# Revit family: Coat_Hook-Bobrick-Fino-B-9542
name_source: partatom
category: Specialty Equipment
revit_build: Autodesk Revit 2018 (Build: 20170223_1515(x64)
units: mm (PartAtom-declared; Revit-internal decimal feet)

## family parameters
Cut with Voids When Loaded = No
Host = Face
OmniClass Number = 23.40.20.21.31
OmniClass Title = Robe Hooks
Part Type = Normal
Room Calculation Point = No
Round Connector Dimension = Use Diameter
Shared = Yes

## types (1)
- B-9542
    Assembly Code = C1030200
    Default Elevation = 0 "
    Description = Fino Collection Surface Mounted Coat Hook
    Finish = Stainless_Steel-Bobrick-Type_303-Satin_Finish
    Flange Cover Diameter = 1.34 "
    Hook Pin Diameter = 0.64 "
    Installation Type = Wall Mounted
    Length = 2.5 "
    Manufacturer = Bobrick
    Material = Stainless_Steel-Bobrick-Type_303-Satin_Finish
    Model = B-9542
    Post Diameter = 0.75 "
    Price = Prices may vary. Please consult Manufacturer Representative for most up-to-date price list.
    URL = https://www.bobrick.com

## geometry (parser evidence)
native form markers: Sweep x3
no freeform markers — native parametric forms only
